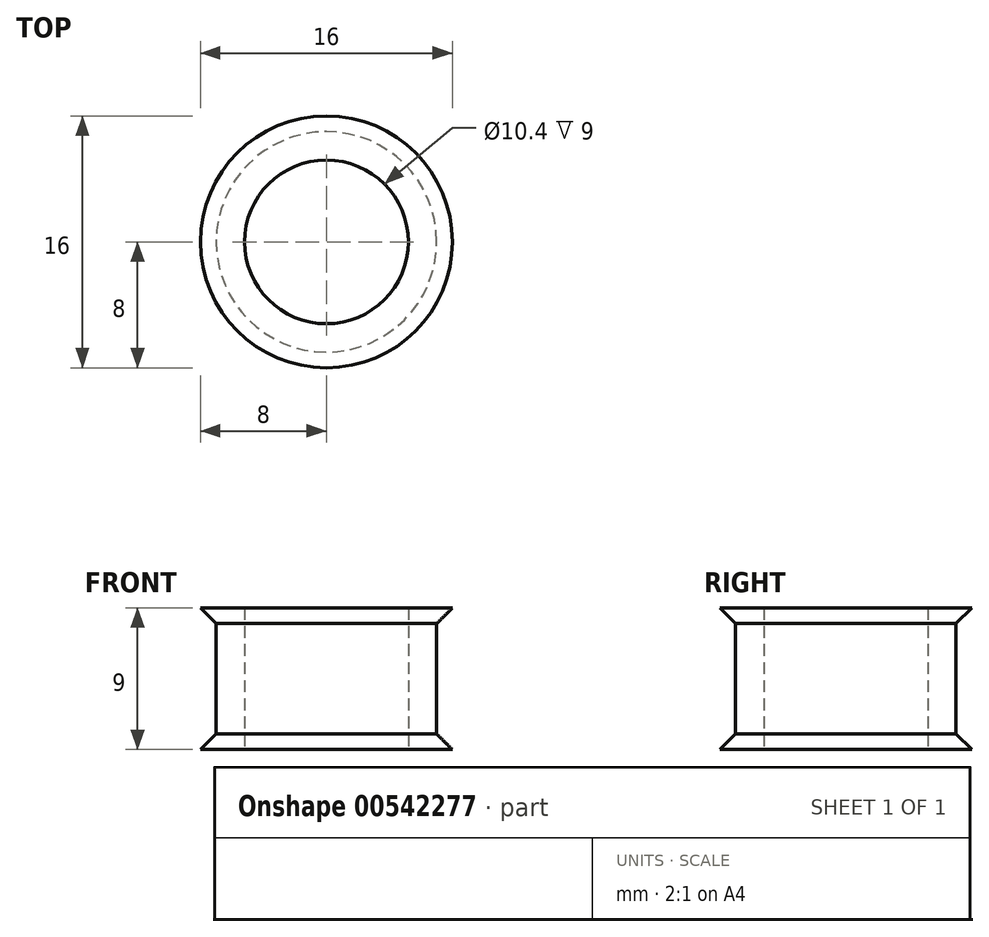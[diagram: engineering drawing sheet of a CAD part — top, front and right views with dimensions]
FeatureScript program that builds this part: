
annotation { "Feature Type Name" : "Feature", "Feature Type Description" : "" }
export const myFeature = defineFeature(function(context is Context, id is Id, definition is map)
    precondition{}
    {
        {
            var Q0;
            Q0=qCreatedBy(makeId("Top.planeOp"),FACE);
            var sketch = newSketch(context, id + "F0", { "sketchPlane" : qUnion([Q0])});
            skCircle(sketch, "E0", {"center": v(0, 0) * mm, "radius": 5.2 * mm});
            skCircle(sketch, "E1", {"center": v(0, 0) * mm, "radius": 8 * mm});
            skCircle(sketch, "E2", {"center": v(0, 0) * mm, "radius": 7 * mm});
            skSolve(sketch);
        }
        {
            var Q0;
            Q0=makeQuery(id+"F0.imprint","IMPRINT",FACE,{"disambiguationData":[TD([[makeQuery(id+"F0.imprint","IMPRINT",EDGE,{"derivedFrom":sQuery(id+"F0.wireOp",EDGE,"E0")}),-1.0]])]});
            extrude(context, id + "F1", {"entities" : qUnion([Q0]), "depth" : 9 * mm, "offsetDistance" : 25 * mm});
        }
        {
            var Q0;
            Q0=makeQuery(id+"F0.imprint","IMPRINT",FACE,{"disambiguationData":[TD([[makeQuery(id+"F0.imprint","IMPRINT",EDGE,{"derivedFrom":sQuery(id+"F0.wireOp",EDGE,"E1")}),1.0]])]});
            extrude(context, id + "F2", {"entities" : qUnion([Q0]), "operationType" : NewBodyOperationType.ADD, "depth" : 1 * mm, "offsetDistance" : 25 * mm});
        }
        {
            var Q0;
            Q0=makeQuery(id+"F1.opExtrude","CAP_FACE",FACE,{"disambiguationData":[OSD([sQuery(id+"F0.wireOp",EDGE,"E0"),sQuery(id+"F0.wireOp",EDGE,"E2")])],"isStart":false});
            var sketch = newSketch(context, id + "F3", { "sketchPlane" : qUnion([Q0])});
            skCircle(sketch, "E3", {"center": v(0, 0) * mm, "radius": 8 * mm});
            skSolve(sketch);
        }
        {
            var Q0;
            Q0=makeQuery(id+"F3.imprint","IMPRINT",FACE,{"disambiguationData":[TD([[makeQuery(id+"F3.imprint","IMPRINT",EDGE,{"derivedFrom":sQuery(id+"F3.wireOp",EDGE,"E3")}),1.0]])]});
            extrude(context, id + "F4", {"entities" : qUnion([Q0]), "operationType" : NewBodyOperationType.ADD, "oppositeDirection" : true, "depth" : 1 * mm, "offsetDistance" : 25 * mm});
        }
        {
            var Q0;
            Q0=makeQuery(id+"F4.opExtrude","CAP_EDGE",EDGE,{"disambiguationData":[OSD([sQuery(id+"F3.wireOp",EDGE,"E3")])],"isStart":false});
            var Q1;
            Q1=makeQuery(id+"F2.opExtrude","CAP_EDGE",EDGE,{"disambiguationData":[OSD([sQuery(id+"F0.wireOp",EDGE,"E1")])],"isStart":false});
            chamfer(context, id + "F5", {"entities" : qUnion([Q0, Q1]), "width" : 1 * mm, "tangentPropagation" : true});
        }
    });
